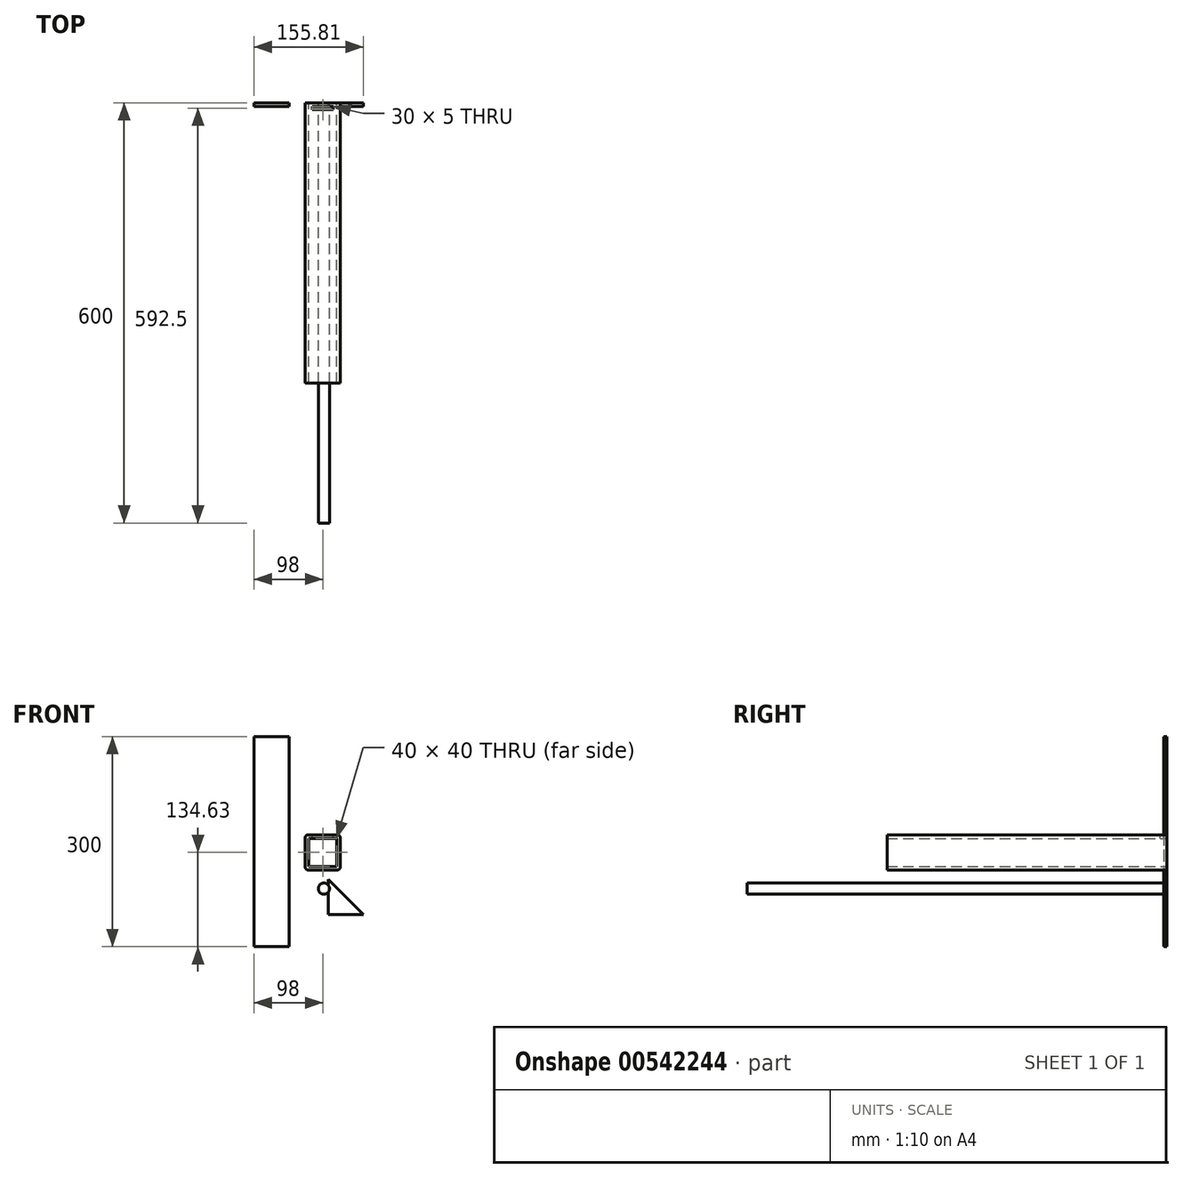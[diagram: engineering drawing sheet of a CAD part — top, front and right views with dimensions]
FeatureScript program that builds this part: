
annotation { "Feature Type Name" : "Feature", "Feature Type Description" : "" }
export const myFeature = defineFeature(function(context is Context, id is Id, definition is map)
    precondition{}
    {
        {
            var Q0;
            Q0=qCreatedBy(makeId("Front.planeOp"),FACE);
            var sketch = newSketch(context, id + "F0", { "sketchPlane" : qUnion([Q0])});
            skLineSegment(sketch, "E0.bottom", {"start": v(4, 0) * mm, "end": v(46, 0) * mm});
            skLineSegment(sketch, "E0.top", {"start": v(4, 50) * mm, "end": v(46, 50) * mm});
            skLineSegment(sketch, "E0.left", {"start": v(0, 4) * mm, "end": v(0, 46) * mm});
            skLineSegment(sketch, "E0.right", {"start": v(50, 4) * mm, "end": v(50, 46) * mm});
            skLineSegment(sketch, "E1.0", {"start": v(5, 45) * mm, "end": v(45, 45) * mm});
            skLineSegment(sketch, "E1.1", {"start": v(5, 5) * mm, "end": v(5, 45) * mm});
            skLineSegment(sketch, "E1.2", {"start": v(5, 5) * mm, "end": v(45, 5) * mm});
            skLineSegment(sketch, "E1.3", {"start": v(45, 5) * mm, "end": v(45, 45) * mm});
            skPoint(sketch, "E2.visualSharp", {"position": v(0, 50) * mm});
            skArc(sketch, "E2.filletArc", {"start": v(4, 50) * mm, "mid": v(1.17, 48.83) * mm, "end": v(0, 46) * mm});
            skPoint(sketch, "E3.visualSharp", {"position": v(0, 0) * mm});
            skArc(sketch, "E3.filletArc", {"start": v(0, 4) * mm, "mid": v(1.17, 1.17) * mm, "end": v(4, 0) * mm});
            skPoint(sketch, "E4.visualSharp", {"position": v(50, 0) * mm});
            skArc(sketch, "E4.filletArc", {"start": v(46, 0) * mm, "mid": v(48.83, 1.17) * mm, "end": v(50, 4) * mm});
            skPoint(sketch, "E5.visualSharp", {"position": v(50, 50) * mm});
            skArc(sketch, "E5.filletArc", {"start": v(50, 46) * mm, "mid": v(48.83, 48.83) * mm, "end": v(46, 50) * mm});
            skSolve(sketch);
        }
        {
            var Q0;
            Q0 = qSketchRegion(id + "F0", true);
            extrude(context, id + "F1", {"entities" : qUnion([Q0]), "depth" : 400 * mm, "offsetDistance" : 25 * mm});
        }
        {
            var Q0;
            Q0=qCreatedBy(makeId("Front.planeOp"),FACE);
            var sketch = newSketch(context, id + "F2", { "sketchPlane" : qUnion([Q0])});
            skLineSegment(sketch, "E6.bottom", {"start": v(-73, 190.37) * mm, "end": v(-23, 190.37) * mm});
            skLineSegment(sketch, "E6.top", {"start": v(-73, -109.63) * mm, "end": v(-23, -109.63) * mm});
            skLineSegment(sketch, "E6.left", {"start": v(-73, 190.37) * mm, "end": v(-73, -109.63) * mm});
            skLineSegment(sketch, "E6.right", {"start": v(-23, 190.37) * mm, "end": v(-23, -109.63) * mm});
            skSolve(sketch);
        }
        {
            var Q0;
            Q0 = qSketchRegion(id + "F2", true);
            extrude(context, id + "F3", {"entities" : qUnion([Q0]), "depth" : 5 * mm, "offsetDistance" : 25 * mm});
        }
        {
            var Q0;
            Q0=qCreatedBy(makeId("Front.planeOp"),FACE);
            var sketch = newSketch(context, id + "F4", { "sketchPlane" : qUnion([Q0])});
            skCircle(sketch, "E7", {"center": v(26.67, -26.67) * mm, "radius": 8 * mm});
            skSolve(sketch);
        }
        {
            var Q0;
            Q0 = qSketchRegion(id + "F4", true);
            extrude(context, id + "F5", {"entities" : qUnion([Q0]), "depth" : 600 * mm, "offsetDistance" : 25 * mm});
        }
        {
            var Q0;
            Q0=qCreatedBy(makeId("Front.planeOp"),FACE);
            var sketch = newSketch(context, id + "F6", { "sketchPlane" : qUnion([Q0])});
            skLineSegment(sketch, "E8", {"start": v(32.81, -63.81) * mm, "end": v(82.81, -63.81) * mm});
            skLineSegment(sketch, "E9", {"start": v(82.81, -63.81) * mm, "end": v(32.81, -13.81) * mm});
            skLineSegment(sketch, "E10", {"start": v(32.81, -13.81) * mm, "end": v(32.81, -63.81) * mm});
            skSolve(sketch);
        }
        {
            var Q0;
            Q0 = qSketchRegion(id + "F6", true);
            extrude(context, id + "F7", {"entities" : qUnion([Q0]), "depth" : 5 * mm, "offsetDistance" : 25 * mm});
        }
        {
            var Q0;
            Q0=makeQuery(id+"F1.opExtrude","SWEPT_FACE",FACE,{"disambiguationData":[OSD([sQuery(id+"F0.wireOp",EDGE,"E0.top")])]});
            var sketch = newSketch(context, id + "F8", { "sketchPlane" : qUnion([Q0])});
            skLineSegment(sketch, "E11.bottom", {"start": v(10, -5) * mm, "end": v(40, -5) * mm});
            skLineSegment(sketch, "E11.top", {"start": v(10, -10) * mm, "end": v(40, -10) * mm});
            skLineSegment(sketch, "E11.left", {"start": v(10, -5) * mm, "end": v(10, -10) * mm});
            skLineSegment(sketch, "E11.right", {"start": v(40, -5) * mm, "end": v(40, -10) * mm});
            skSolve(sketch);
        }
        {
            var Q0;
            Q0 = qSketchRegion(id + "F8", true);
            extrude(context, id + "F9", {"entities" : qUnion([Q0]), "operationType" : NewBodyOperationType.REMOVE, "endBound" : BoundingType.UP_TO_NEXT, "oppositeDirection" : true, "depth" : 25 * mm, "offsetDistance" : 25 * mm});
        }
    });
